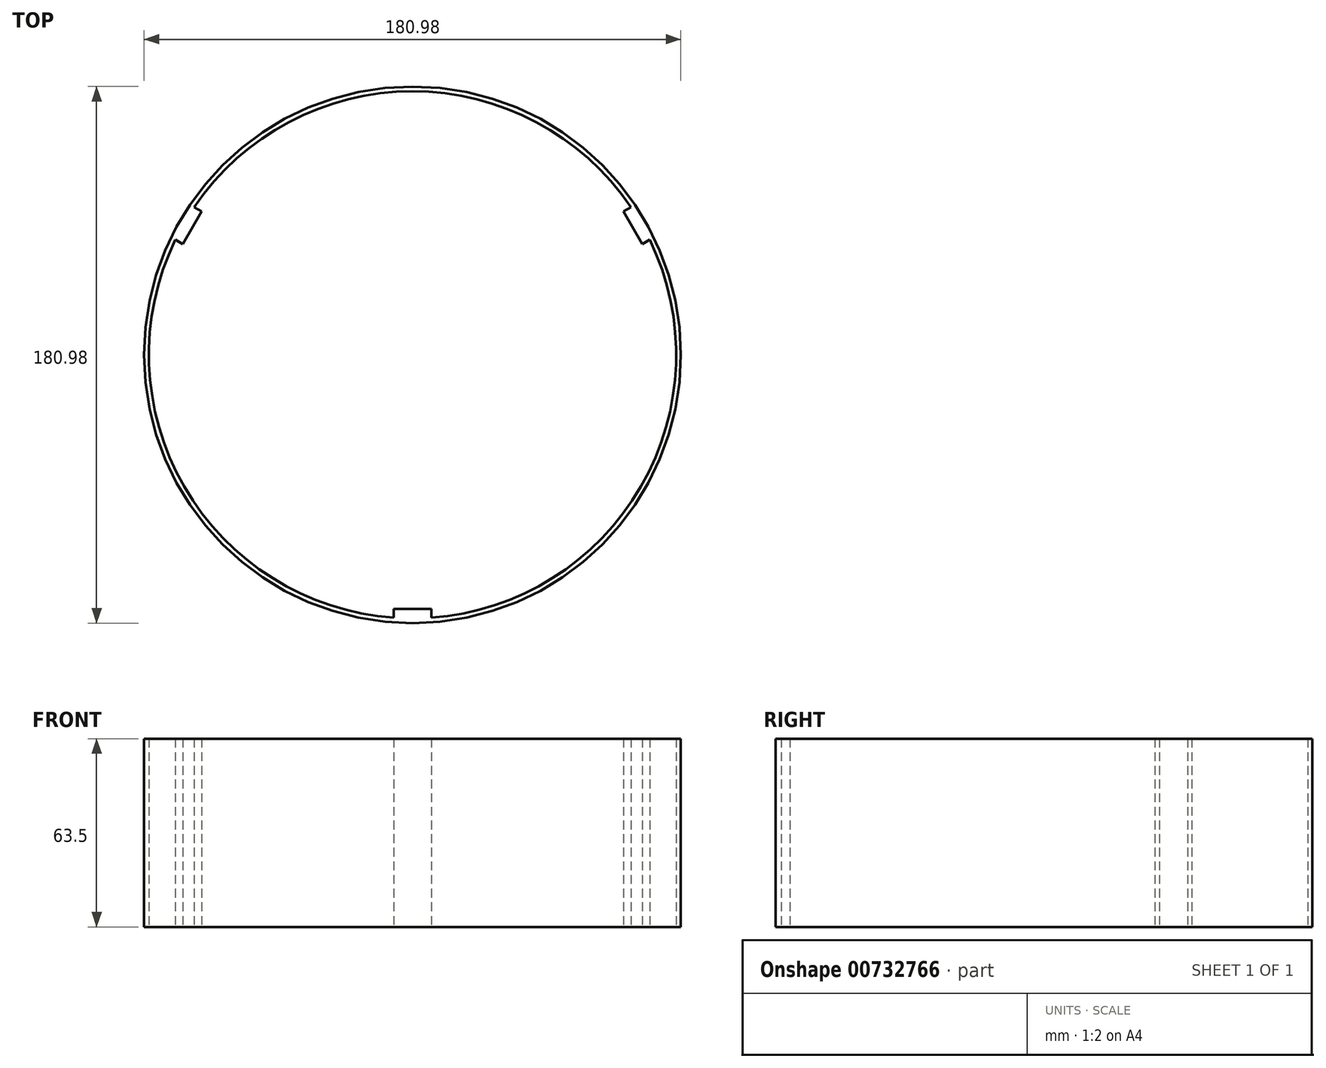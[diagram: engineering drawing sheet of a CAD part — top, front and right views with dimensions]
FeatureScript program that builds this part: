
annotation { "Feature Type Name" : "Feature", "Feature Type Description" : "" }
export const myFeature = defineFeature(function(context is Context, id is Id, definition is map)
    precondition{}
    {
        {
            var Q0;
            Q0=qCreatedBy(makeId("Top.planeOp"),FACE);
            var sketch = newSketch(context, id + "F0", { "sketchPlane" : qUnion([Q0])});
            skCircle(sketch, "E0", {"center": v(0, 0) * mm, "radius": 90.49 * mm});
            skArc(sketch, "E1.0", {"start": v(-79.97, 38.84) * mm, "mid": v(-76.99, -44.45) * mm, "end": v(-6.35, -88.67) * mm});
            skLineSegment(sketch, "E2", {"start": v(0, 0) * mm, "end": v(0, -92.75) * mm, "construction": true});
            skLineSegment(sketch, "E3", {"start": v(0, 0) * mm, "end": v(105.18, 60.73) * mm, "construction": true});
            skLineSegment(sketch, "E4", {"start": v(0, 0) * mm, "end": v(-116.6, 67.32) * mm, "construction": true});
            skLineSegment(sketch, "E5", {"start": v(-74.24, 42.86) * mm, "end": v(-71.07, 48.36) * mm});
            skLineSegment(sketch, "E6", {"start": v(-71.07, 48.36) * mm, "end": v(-73.62, 49.84) * mm});
            skLineSegment(sketch, "E7", {"start": v(-74.24, 42.86) * mm, "end": v(-77.42, 37.36) * mm});
            skLineSegment(sketch, "E8", {"start": v(-77.42, 37.36) * mm, "end": v(-79.97, 38.84) * mm});
            skLineSegment(sketch, "E9", {"start": v(0, -85.73) * mm, "end": v(-6.35, -85.73) * mm});
            skLineSegment(sketch, "E10", {"start": v(-6.35, -85.73) * mm, "end": v(-6.35, -88.67) * mm});
            skLineSegment(sketch, "E11", {"start": v(0, -85.73) * mm, "end": v(6.35, -85.73) * mm});
            skLineSegment(sketch, "E12", {"start": v(6.35, -85.73) * mm, "end": v(6.35, -88.67) * mm});
            skLineSegment(sketch, "E13", {"start": v(74.24, 42.86) * mm, "end": v(71.07, 48.36) * mm});
            skLineSegment(sketch, "E14", {"start": v(71.07, 48.36) * mm, "end": v(73.62, 49.84) * mm});
            skLineSegment(sketch, "E15", {"start": v(74.24, 42.86) * mm, "end": v(77.42, 37.36) * mm});
            skLineSegment(sketch, "E16", {"start": v(77.42, 37.36) * mm, "end": v(79.97, 38.84) * mm});
            skArc(sketch, "E17.trimOffspring", {"start": v(73.62, 49.84) * mm, "mid": v(0, 88.9) * mm, "end": v(-73.62, 49.84) * mm});
            skArc(sketch, "E18.trimOffspring", {"start": v(6.35, -88.67) * mm, "mid": v(76.99, -44.45) * mm, "end": v(79.97, 38.84) * mm});
            skSolve(sketch);
        }
        {
            var Q0;
            Q0=makeQuery(id+"F0.imprint","IMPRINT",FACE,{"disambiguationData":[TD([[makeQuery(id+"F0.imprint","IMPRINT",EDGE,{"derivedFrom":sQuery(id+"F0.wireOp",EDGE,"E0")}),1.0]])]});
            extrude(context, id + "F1", {"entities" : qUnion([Q0]), "depth" : 63.5 * mm, "offsetDistance" : 25.4 * mm});
        }
    });
